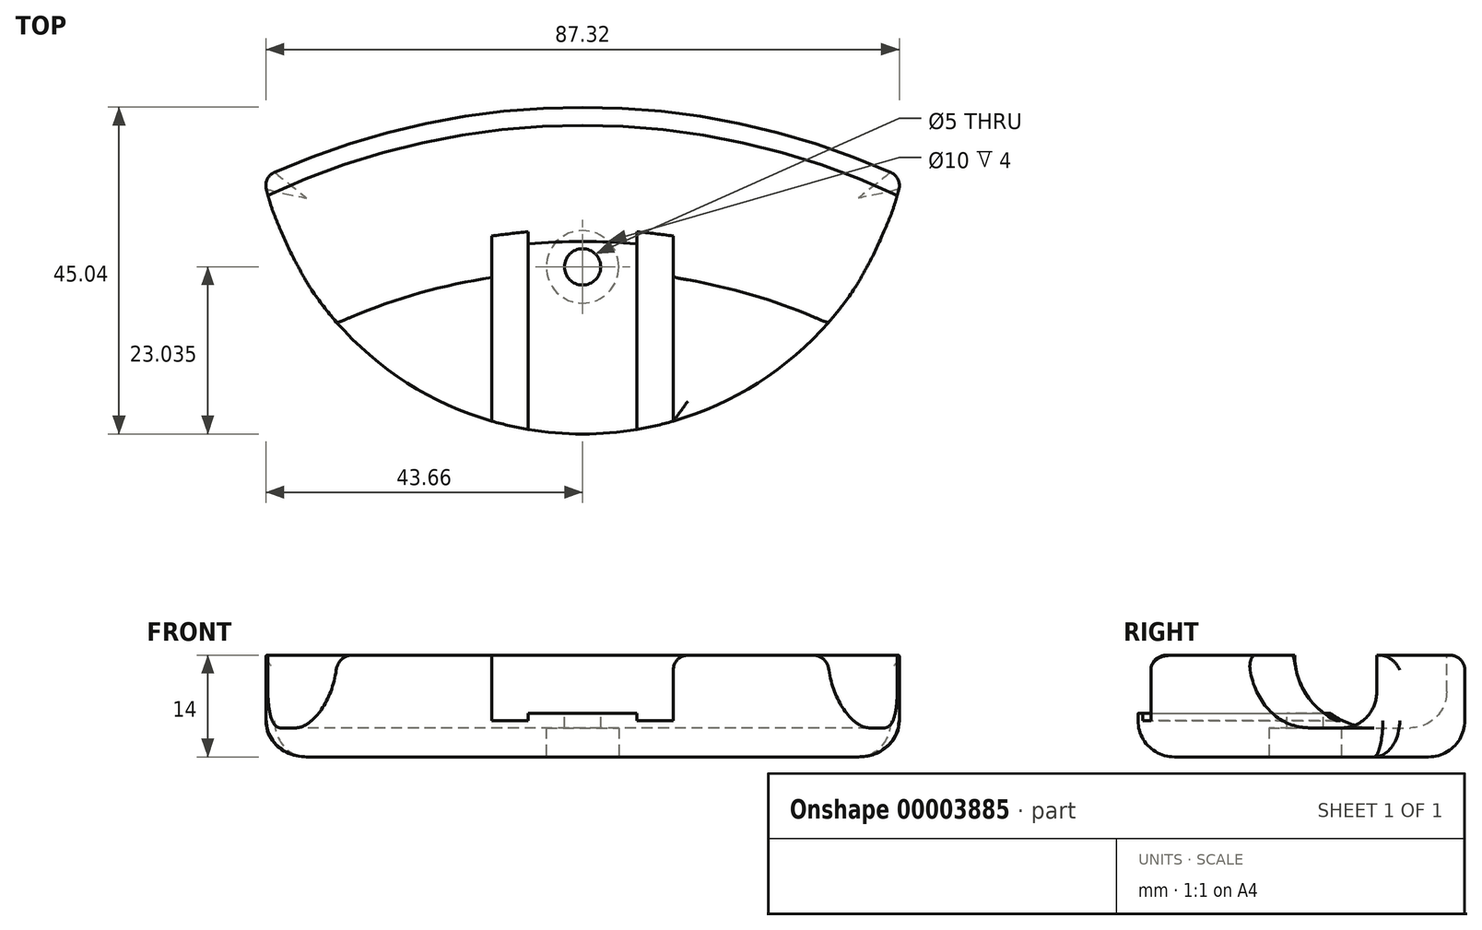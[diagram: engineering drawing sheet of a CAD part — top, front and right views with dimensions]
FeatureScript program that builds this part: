
annotation { "Feature Type Name" : "Feature", "Feature Type Description" : "" }
export const myFeature = defineFeature(function(context is Context, id is Id, definition is map)
    precondition{}
    {
        {
            var Q0;
            Q0=qCreatedBy(makeId("Top.planeOp"),FACE);
            var sketch = newSketch(context, id + "F0", { "sketchPlane" : qUnion([Q0])});
            skLineSegment(sketch, "E0.bottom", {"start": v(-12.5, 20) * mm, "end": v(12.5, 20) * mm});
            skLineSegment(sketch, "E0.top", {"start": v(-12.5, -20) * mm, "end": v(12.5, -20) * mm});
            skLineSegment(sketch, "E0.left", {"start": v(-12.5, 20) * mm, "end": v(-12.5, -20) * mm});
            skLineSegment(sketch, "E0.right", {"start": v(12.5, 20) * mm, "end": v(12.5, -20) * mm});
            skArc(sketch, "E1", {"start": v(43.99, 13.6) * mm, "mid": v(0, 23.27) * mm, "end": v(-43.99, 13.6) * mm});
            skArc(sketch, "E2", {"start": v(-43.99, 13.6) * mm, "mid": v(0, -21.77) * mm, "end": v(43.99, 13.6) * mm});
            skPoint(sketch, "E3", {"position": v(-43.99, 13.6) * mm});
            skPoint(sketch, "E4", {"position": v(43.99, 13.6) * mm});
            skPoint(sketch, "E5", {"position": v(-43.37, 11.14) * mm});
            skPoint(sketch, "E6", {"position": v(43.37, 11.14) * mm});
            skArc(sketch, "E7.trimOffspring", {"start": v(43.37, 11.14) * mm, "mid": v(0, 20.77) * mm, "end": v(-43.37, 11.14) * mm});
            skLineSegment(sketch, "E8", {"start": v(0, 20) * mm, "end": v(0, -20) * mm, "construction": true});
            skArc(sketch, "E9", {"start": v(33.81, -6.48) * mm, "mid": v(0, 0.77) * mm, "end": v(-33.81, -6.48) * mm});
            skPoint(sketch, "E10", {"position": v(0, 1.27) * mm});
            skCircle(sketch, "E11", {"center": v(0, 1.27) * mm, "radius": 2.5 * mm});
            skLineSegment(sketch, "E12", {"start": v(-7.5, -12.17) * mm, "end": v(7.5, -12.17) * mm, "construction": true});
            skPoint(sketch, "E13", {"position": v(0, -12.17) * mm});
            skLineSegment(sketch, "E14", {"start": v(-7.5, -21.14) * mm, "end": v(-7.5, 10.15) * mm});
            skLineSegment(sketch, "E15", {"start": v(7.5, -21.14) * mm, "end": v(7.5, 10.15) * mm});
            skLineSegment(sketch, "E16", {"start": v(-7.5, 10.15) * mm, "end": v(7.5, 10.15) * mm});
            skSolve(sketch);
        }
        {
            var Q0;
            Q0=makeQuery(id+"F0.imprint","IMPRINT",FACE,{"disambiguationData":[TD([[makeQuery(id+"F0.imprint","IMPRINT",EDGE,{"derivedFrom":sQuery(id+"F0.wireOp",EDGE,"E1")}),1.0]])]});
            var Q1;
            {var subQ1=sQuery(id+"F0.wireOp",EDGE,"E7.trimOffspring");Q1=makeQuery(id+"F0.imprint","IMPRINT",FACE,{"disambiguationData":[TD([[makeQuery(id+"F0.imprint","IMPRINT",EDGE,{"derivedFrom":subQ1}),1.0]])]});}
            var Q2;
            {var subQ0=sQuery(id+"F0.wireOp",EDGE,"E9");Q2=makeQuery(id+"F0.imprint","IMPRINT",FACE,{"disambiguationData":[TD([[makeQuery(id+"F0.imprint","IMPRINT",EDGE,{"derivedFrom":subQ0}),1.0]])]});}
            var Q3;
            {var subQ5=sQuery(id+"F0.wireOp",EDGE,"E0.top");Q3=makeQuery(id+"F0.imprint","IMPRINT",FACE,{"disambiguationData":[TD([[makeQuery(id+"F0.imprint","IMPRINT",EDGE,{"derivedFrom":subQ5}),1.0]])]});}
            var Q4;
            {var subQ1=sQuery(id+"F0.wireOp",EDGE,"E0.top");Q4=makeQuery(id+"F0.imprint","IMPRINT",FACE,{"disambiguationData":[TD([[makeQuery(id+"F0.imprint","IMPRINT",EDGE,{"derivedFrom":subQ1}),-1.0]])]});}
            var Q5;
            {var subQ3=sQuery(id+"F0.wireOp",EDGE,"E2");var subQ5=sQuery(id+"F0.wireOp",EDGE,"E7.trimOffspring");var subQ6=makeQuery(id+"F0.imprint","INTERSECT",VERTEX,{"disambiguationData":[OD(0.0)],"derivedFrom":[subQ3,subQ5]});Q5=makeQuery(id+"F0.imprint","IMPRINT",FACE,{"disambiguationData":[TD([[makeQuery(id+"F0.imprint","IMPRINT",EDGE,{"disambiguationData":[TD([[subQ6,1.0]])],"derivedFrom":subQ3}),1.0]])]});}
            var Q6;
            {var subQ5=sQuery(id+"F0.wireOp",EDGE,"E0.bottom");Q6=makeQuery(id+"F0.imprint","IMPRINT",FACE,{"disambiguationData":[TD([[makeQuery(id+"F0.imprint","IMPRINT",EDGE,{"derivedFrom":subQ5}),-1.0]])]});}
            var Q7;
            {var subQ3=sQuery(id+"F0.wireOp",EDGE,"E2");var subQ5=sQuery(id+"F0.wireOp",EDGE,"E7.trimOffspring");var subQ6=makeQuery(id+"F0.imprint","INTERSECT",VERTEX,{"disambiguationData":[OD(1.0)],"derivedFrom":[subQ3,subQ5]});Q7=makeQuery(id+"F0.imprint","IMPRINT",FACE,{"disambiguationData":[TD([[makeQuery(id+"F0.imprint","IMPRINT",EDGE,{"disambiguationData":[TD([[subQ6,-1.0]])],"derivedFrom":subQ3}),1.0]])]});}
            var Q8;
            {var subQ0=sQuery(id+"F0.wireOp",EDGE,"E11");var subQ1=sQuery(id+"F0.wireOp",EDGE,"E9");var subQ3=makeQuery(id+"F0.imprint","INTERSECT",VERTEX,{"disambiguationData":[OD(0.0)],"derivedFrom":[subQ1,subQ0]});Q8=makeQuery(id+"F0.imprint","IMPRINT",FACE,{"disambiguationData":[TD([[makeQuery(id+"F0.imprint","IMPRINT",EDGE,{"disambiguationData":[TD([[subQ3,-1.0]])],"derivedFrom":subQ1}),-1.0]])]});}
            var Q9;
            {var subQ0=sQuery(id+"F0.wireOp",EDGE,"E11");var subQ1=sQuery(id+"F0.wireOp",EDGE,"E9");var subQ3=makeQuery(id+"F0.imprint","INTERSECT",VERTEX,{"disambiguationData":[OD(0.0)],"derivedFrom":[subQ1,subQ0]});Q9=makeQuery(id+"F0.imprint","IMPRINT",FACE,{"disambiguationData":[TD([[makeQuery(id+"F0.imprint","IMPRINT",EDGE,{"disambiguationData":[TD([[subQ3,-1.0]])],"derivedFrom":subQ1}),1.0]])]});}
            var Q10;
            {var subQ0=sQuery(id+"F0.wireOp",EDGE,"E9");var subQ3=sQuery(id+"F0.wireOp",EDGE,"E2");var subQ4=makeQuery(id+"F0.imprint","INTERSECT",VERTEX,{"disambiguationData":[OD(1.0)],"derivedFrom":[subQ3,subQ0]});Q10=makeQuery(id+"F0.imprint","IMPRINT",FACE,{"disambiguationData":[TD([[makeQuery(id+"F0.imprint","IMPRINT",EDGE,{"disambiguationData":[TD([[subQ4,1.0]])],"derivedFrom":subQ0}),1.0]])]});}
            var Q11;
            {var subQ0=sQuery(id+"F0.wireOp",EDGE,"E9");var subQ3=sQuery(id+"F0.wireOp",EDGE,"E2");var subQ4=makeQuery(id+"F0.imprint","INTERSECT",VERTEX,{"disambiguationData":[OD(0.0)],"derivedFrom":[subQ3,subQ0]});Q11=makeQuery(id+"F0.imprint","IMPRINT",FACE,{"disambiguationData":[TD([[makeQuery(id+"F0.imprint","IMPRINT",EDGE,{"disambiguationData":[TD([[subQ4,-1.0]])],"derivedFrom":subQ0}),1.0]])]});}
            var Q12;
            {var subQ4=sQuery(id+"F0.wireOp",EDGE,"f2ed5ddf-1e71-4b46-be9b-5d21263913f5.bottom");Q12=makeQuery(id+"F0.imprint","IMPRINT",FACE,{"disambiguationData":[TD([[makeQuery(id+"F0.imprint","IMPRINT",EDGE,{"derivedFrom":subQ4}),-1.0]])]});}
            var Q13;
            {var subQ0=sQuery(id+"F0.wireOp",EDGE,"f2ed5ddf-1e71-4b46-be9b-5d21263913f5.top");Q13=makeQuery(id+"F0.imprint","IMPRINT",FACE,{"disambiguationData":[TD([[makeQuery(id+"F0.imprint","IMPRINT",EDGE,{"derivedFrom":subQ0}),1.0]])]});}
            var Q14;
            {var subQ1=sQuery(id+"F0.wireOp",EDGE,"E0.bottom");var subQ5=sQuery(id+"F0.wireOp",EDGE,"E14");var subQ6=makeQuery(id+"F0.imprint","INTERSECT",VERTEX,{"derivedFrom":[subQ1,subQ5]});Q14=makeQuery(id+"F0.imprint","IMPRINT",FACE,{"disambiguationData":[TD([[makeQuery(id+"F0.imprint","IMPRINT",EDGE,{"disambiguationData":[TD([[subQ6,-1.0]])],"derivedFrom":subQ1}),1.0]])]});}
            var Q15;
            {var subQ3=sQuery(id+"F0.wireOp",EDGE,"E0.bottom");var subQ8=sQuery(id+"F0.wireOp",EDGE,"E14");var subQ10=makeQuery(id+"F0.imprint","INTERSECT",VERTEX,{"derivedFrom":[subQ3,subQ8]});Q15=makeQuery(id+"F0.imprint","IMPRINT",FACE,{"disambiguationData":[TD([[makeQuery(id+"F0.imprint","IMPRINT",EDGE,{"disambiguationData":[TD([[subQ10,-1.0]])],"derivedFrom":subQ3}),-1.0]])]});}
            var Q16;
            {var subQ3=sQuery(id+"F0.wireOp",EDGE,"E0.top");var subQ5=sQuery(id+"F0.wireOp",EDGE,"E14");var subQ7=makeQuery(id+"F0.imprint","INTERSECT",VERTEX,{"derivedFrom":[subQ3,subQ5]});Q16=makeQuery(id+"F0.imprint","IMPRINT",FACE,{"disambiguationData":[TD([[makeQuery(id+"F0.imprint","IMPRINT",EDGE,{"disambiguationData":[TD([[subQ7,-1.0]])],"derivedFrom":subQ3}),1.0]])]});}
            var Q17;
            {var subQ0=sQuery(id+"F0.wireOp",EDGE,"E14");var subQ1=sQuery(id+"F0.wireOp",EDGE,"E0.top");var subQ2=makeQuery(id+"F0.imprint","INTERSECT",VERTEX,{"derivedFrom":[subQ1,subQ0]});Q17=makeQuery(id+"F0.imprint","IMPRINT",FACE,{"disambiguationData":[TD([[makeQuery(id+"F0.imprint","IMPRINT",EDGE,{"disambiguationData":[TD([[subQ2,-1.0]])],"derivedFrom":subQ1}),-1.0]])]});}
            var Q18;
            {var subQ3=sQuery(id+"F0.wireOp",EDGE,"E16");Q18=makeQuery(id+"F0.imprint","IMPRINT",FACE,{"disambiguationData":[TD([[makeQuery(id+"F0.imprint","IMPRINT",EDGE,{"derivedFrom":subQ3}),-1.0]])]});}
            extrude(context, id + "F1", {"entities" : qUnion([Q0, Q1, Q2, Q3, Q4, Q5, Q6, Q7, Q8, Q9, Q10, Q11, Q12, Q13, Q14, Q15, Q16, Q17, Q18]), "oppositeDirection" : true, "depth" : 14 * mm});
        }
        {
            var Q0;
            {var subQ1=sQuery(id+"F0.wireOp",EDGE,"E7.trimOffspring");Q0=makeQuery(id+"F0.imprint","IMPRINT",FACE,{"disambiguationData":[TD([[makeQuery(id+"F0.imprint","IMPRINT",EDGE,{"derivedFrom":subQ1}),1.0]])]});}
            var Q1;
            {var subQ3=sQuery(id+"F0.wireOp",EDGE,"E2");var subQ5=sQuery(id+"F0.wireOp",EDGE,"E7.trimOffspring");var subQ6=makeQuery(id+"F0.imprint","INTERSECT",VERTEX,{"disambiguationData":[OD(0.0)],"derivedFrom":[subQ3,subQ5]});Q1=makeQuery(id+"F0.imprint","IMPRINT",FACE,{"disambiguationData":[TD([[makeQuery(id+"F0.imprint","IMPRINT",EDGE,{"disambiguationData":[TD([[subQ6,1.0]])],"derivedFrom":subQ3}),1.0]])]});}
            var Q2;
            {var subQ5=sQuery(id+"F0.wireOp",EDGE,"E0.bottom");Q2=makeQuery(id+"F0.imprint","IMPRINT",FACE,{"disambiguationData":[TD([[makeQuery(id+"F0.imprint","IMPRINT",EDGE,{"derivedFrom":subQ5}),-1.0]])]});}
            var Q3;
            {var subQ3=sQuery(id+"F0.wireOp",EDGE,"E2");var subQ5=sQuery(id+"F0.wireOp",EDGE,"E7.trimOffspring");var subQ6=makeQuery(id+"F0.imprint","INTERSECT",VERTEX,{"disambiguationData":[OD(1.0)],"derivedFrom":[subQ3,subQ5]});Q3=makeQuery(id+"F0.imprint","IMPRINT",FACE,{"disambiguationData":[TD([[makeQuery(id+"F0.imprint","IMPRINT",EDGE,{"disambiguationData":[TD([[subQ6,-1.0]])],"derivedFrom":subQ3}),1.0]])]});}
            var Q4;
            {var subQ4=sQuery(id+"F0.wireOp",EDGE,"f2ed5ddf-1e71-4b46-be9b-5d21263913f5.bottom");Q4=makeQuery(id+"F0.imprint","IMPRINT",FACE,{"disambiguationData":[TD([[makeQuery(id+"F0.imprint","IMPRINT",EDGE,{"derivedFrom":subQ4}),-1.0]])]});}
            var Q5;
            {var subQ0=sQuery(id+"F0.wireOp",EDGE,"E11");var subQ1=sQuery(id+"F0.wireOp",EDGE,"E9");var subQ3=makeQuery(id+"F0.imprint","INTERSECT",VERTEX,{"disambiguationData":[OD(0.0)],"derivedFrom":[subQ1,subQ0]});Q5=makeQuery(id+"F0.imprint","IMPRINT",FACE,{"disambiguationData":[TD([[makeQuery(id+"F0.imprint","IMPRINT",EDGE,{"disambiguationData":[TD([[subQ3,-1.0]])],"derivedFrom":subQ1}),-1.0]])]});}
            var Q6;
            {var subQ3=sQuery(id+"F0.wireOp",EDGE,"E0.bottom");var subQ8=sQuery(id+"F0.wireOp",EDGE,"E14");var subQ10=makeQuery(id+"F0.imprint","INTERSECT",VERTEX,{"derivedFrom":[subQ3,subQ8]});Q6=makeQuery(id+"F0.imprint","IMPRINT",FACE,{"disambiguationData":[TD([[makeQuery(id+"F0.imprint","IMPRINT",EDGE,{"disambiguationData":[TD([[subQ10,-1.0]])],"derivedFrom":subQ3}),-1.0]])]});}
            var Q7;
            {var subQ3=sQuery(id+"F0.wireOp",EDGE,"E16");Q7=makeQuery(id+"F0.imprint","IMPRINT",FACE,{"disambiguationData":[TD([[makeQuery(id+"F0.imprint","IMPRINT",EDGE,{"derivedFrom":subQ3}),-1.0]])]});}
            extrude(context, id + "F2", {"entities" : qUnion([Q0, Q1, Q2, Q3, Q4, Q5, Q6, Q7]), "operationType" : NewBodyOperationType.REMOVE, "oppositeDirection" : true, "depth" : 10 * mm});
        }
        {
            var Q0;
            {var subQ5=sQuery(id+"F0.wireOp",EDGE,"E0.top");Q0=makeQuery(id+"F0.imprint","IMPRINT",FACE,{"disambiguationData":[TD([[makeQuery(id+"F0.imprint","IMPRINT",EDGE,{"derivedFrom":subQ5}),1.0]])]});}
            var Q1;
            {var subQ1=sQuery(id+"F0.wireOp",EDGE,"E0.top");Q1=makeQuery(id+"F0.imprint","IMPRINT",FACE,{"disambiguationData":[TD([[makeQuery(id+"F0.imprint","IMPRINT",EDGE,{"derivedFrom":subQ1}),-1.0]])]});}
            var Q2;
            {var subQ0=sQuery(id+"F0.wireOp",EDGE,"f2ed5ddf-1e71-4b46-be9b-5d21263913f5.top");Q2=makeQuery(id+"F0.imprint","IMPRINT",FACE,{"disambiguationData":[TD([[makeQuery(id+"F0.imprint","IMPRINT",EDGE,{"derivedFrom":subQ0}),1.0]])]});}
            var Q3;
            {var subQ0=sQuery(id+"F0.wireOp",EDGE,"E11");var subQ1=sQuery(id+"F0.wireOp",EDGE,"E9");var subQ3=makeQuery(id+"F0.imprint","INTERSECT",VERTEX,{"disambiguationData":[OD(0.0)],"derivedFrom":[subQ1,subQ0]});Q3=makeQuery(id+"F0.imprint","IMPRINT",FACE,{"disambiguationData":[TD([[makeQuery(id+"F0.imprint","IMPRINT",EDGE,{"disambiguationData":[TD([[subQ3,-1.0]])],"derivedFrom":subQ1}),1.0]])]});}
            extrude(context, id + "F3", {"entities" : qUnion([Q0, Q1, Q2, Q3]), "operationType" : NewBodyOperationType.REMOVE, "oppositeDirection" : true, "depth" : 9 * mm});
        }
        {
            var Q0;
            Q0=makeQuery(id+"F2.boolean.opBoolean","COPY",EDGE,{"derivedFrom":makeQuery(id+"F2.opExtrude","CAP_EDGE",EDGE,{"disambiguationData":[OSD([sQuery(id+"F0.wireOp",EDGE,"E9")])],"isStart":false})});
            fillet(context, id + "F4", {"entities" : qUnion([Q0]), "radius" : 10 * mm, "tangentPropagation" : true, "allowEdgeOverflow" : false});
        }
        {
            var Q0;
            Q0=makeQuery(id+"F1.opExtrude","CAP_EDGE",EDGE,{"disambiguationData":[OSD([sQuery(id+"F0.wireOp",EDGE,"E2")])],"isStart":false});
            var Q1;
            Q1=makeQuery(id+"F1.opExtrude","CAP_EDGE",EDGE,{"disambiguationData":[OSD([sQuery(id+"F0.wireOp",EDGE,"E1")])],"isStart":false});
            fillet(context, id + "F5", {"entities" : qUnion([Q0, Q1]), "radius" : 5 * mm, "tangentPropagation" : true, "allowEdgeOverflow" : false});
        }
        {
            var Q0;
            Q0=makeQuery(id+"F1.opExtrude","CAP_EDGE",EDGE,{"disambiguationData":[OSD([sQuery(id+"F0.wireOp",EDGE,"E1")])],"isStart":true});
            var Q1;
            {var subQ0=sQuery(id+"F0.wireOp",EDGE,"E2");var subQ1=makeQuery(id+"F2.opExtrude","SWEPT_FACE",FACE,{"disambiguationData":[OSD([sQuery(id+"F0.wireOp",EDGE,"E9")])]});var subQ2=makeQuery(id+"F1.opExtrude","SWEPT_FACE",FACE,{"disambiguationData":[OSD([subQ0])]});var subQ3=makeQuery(id+"F1.opExtrude","CAP_FACE",FACE,{"disambiguationData":[OSD([sQuery(id+"F0.wireOp",EDGE,"E1"),subQ0])],"isStart":true});Q1=makeQuery(id+"F3.boolean.opBoolean","SPLIT",EDGE,{"disambiguationData":[TD([makeQuery(id+"F3.opExtrude","SWEPT_FACE",FACE,{"disambiguationData":[OSD([sQuery(id+"F0.wireOp",EDGE,"E0.left")])]})])],"derivedFrom":makeQuery(id+"F2.boolean.opBoolean","SPLIT",EDGE,{"disambiguationData":[TD([subQ3,subQ2,subQ1])],"derivedFrom":makeQuery(id+"F1.opExtrude","CAP_EDGE",EDGE,{"disambiguationData":[OSD([subQ0])],"isStart":true})})});}
            var Q2;
            {var subQ0=sQuery(id+"F0.wireOp",EDGE,"E2");var subQ1=makeQuery(id+"F2.opExtrude","SWEPT_FACE",FACE,{"disambiguationData":[OSD([sQuery(id+"F0.wireOp",EDGE,"E9")])]});var subQ2=makeQuery(id+"F1.opExtrude","SWEPT_FACE",FACE,{"disambiguationData":[OSD([subQ0])]});var subQ3=makeQuery(id+"F1.opExtrude","CAP_FACE",FACE,{"disambiguationData":[OSD([sQuery(id+"F0.wireOp",EDGE,"E1"),subQ0])],"isStart":true});Q2=makeQuery(id+"F3.boolean.opBoolean","SPLIT",EDGE,{"disambiguationData":[TD([makeQuery(id+"F3.opExtrude","SWEPT_FACE",FACE,{"disambiguationData":[OSD([sQuery(id+"F0.wireOp",EDGE,"E0.right")])]})])],"derivedFrom":makeQuery(id+"F2.boolean.opBoolean","SPLIT",EDGE,{"disambiguationData":[TD([subQ3,subQ2,subQ1])],"derivedFrom":makeQuery(id+"F1.opExtrude","CAP_EDGE",EDGE,{"disambiguationData":[OSD([subQ0])],"isStart":true})})});}
            var Q3;
            Q3=makeQuery(id+"F3.boolean.opBoolean","COPY",EDGE,{"derivedFrom":makeQuery(id+"F3.opExtrude","SWEPT_EDGE",EDGE,{"disambiguationData":[OSD([sQuery(id+"F0.wireOp",EDGE,"E0.top"),sQuery(id+"F0.wireOp",EDGE,"E0.right"),sQuery(id+"F0.wireOp",EDGE,"E2")])]})});
            var Q4;
            Q4=makeQuery(id+"F3.boolean.opBoolean","COPY",EDGE,{"derivedFrom":makeQuery(id+"F3.opExtrude","SWEPT_EDGE",EDGE,{"disambiguationData":[OSD([sQuery(id+"F0.wireOp",EDGE,"E0.top"),sQuery(id+"F0.wireOp",EDGE,"E0.left"),sQuery(id+"F0.wireOp",EDGE,"E2")])]})});
            var Q5;
            Q5=makeQuery(id+"F3.boolean.opBoolean","COPY",EDGE,{"derivedFrom":makeQuery(id+"F3.opExtrude","CAP_EDGE",EDGE,{"disambiguationData":[OSD([sQuery(id+"F0.wireOp",EDGE,"E0.left")])],"isStart":true})});
            var Q6;
            Q6=makeQuery(id+"F3.boolean.opBoolean","COPY",EDGE,{"derivedFrom":makeQuery(id+"F3.opExtrude","CAP_EDGE",EDGE,{"disambiguationData":[OSD([sQuery(id+"F0.wireOp",EDGE,"E0.right")])],"isStart":true})});
            var Q7;
            {var subQ0=sQuery(id+"F0.wireOp",EDGE,"E9");Q7=makeQuery(id+"F3.boolean.opBoolean","SPLIT",EDGE,{"disambiguationData":[TD([makeQuery(id+"F3.opExtrude","SWEPT_FACE",FACE,{"disambiguationData":[OSD([sQuery(id+"F0.wireOp",EDGE,"E0.left")])]})])],"derivedFrom":makeQuery(id+"F2.boolean.opBoolean","COPY",EDGE,{"derivedFrom":makeQuery(id+"F2.opExtrude","CAP_EDGE",EDGE,{"disambiguationData":[OSD([subQ0])],"isStart":true})})});}
            var Q8;
            {var subQ0=sQuery(id+"F0.wireOp",EDGE,"E9");Q8=makeQuery(id+"F3.boolean.opBoolean","SPLIT",EDGE,{"disambiguationData":[TD([makeQuery(id+"F3.opExtrude","SWEPT_FACE",FACE,{"disambiguationData":[OSD([sQuery(id+"F0.wireOp",EDGE,"E0.right")])]})])],"derivedFrom":makeQuery(id+"F2.boolean.opBoolean","COPY",EDGE,{"derivedFrom":makeQuery(id+"F2.opExtrude","CAP_EDGE",EDGE,{"disambiguationData":[OSD([subQ0])],"isStart":true})})});}
            var Q9;
            Q9=makeQuery(id+"F2.boolean.opBoolean","COPY",EDGE,{"derivedFrom":makeQuery(id+"F2.opExtrude","CAP_EDGE",EDGE,{"disambiguationData":[OSD([sQuery(id+"F0.wireOp",EDGE,"E7.trimOffspring")])],"isStart":true})});
            var Q10;
            {var subQ0=sQuery(id+"F0.wireOp",EDGE,"E1");var subQ1=sQuery(id+"F0.wireOp",EDGE,"E2");Q10=makeQuery(id+"F1.opExtrude","SWEPT_EDGE",EDGE,{"disambiguationData":[OSD([subQ0,subQ1]),TDD([makeQuery(id+"F0.imprint","INTERSECT",VERTEX,{"disambiguationData":[OD(1.0)],"derivedFrom":[subQ0,subQ1]})])]});}
            var Q11;
            {var subQ0=sQuery(id+"F0.wireOp",EDGE,"E1");var subQ1=sQuery(id+"F0.wireOp",EDGE,"E2");Q11=makeQuery(id+"F1.opExtrude","SWEPT_EDGE",EDGE,{"disambiguationData":[OSD([subQ0,subQ1]),TDD([makeQuery(id+"F0.imprint","INTERSECT",VERTEX,{"disambiguationData":[OD(0.0)],"derivedFrom":[subQ0,subQ1]})])]});}
            fillet(context, id + "F6", {"entities" : qUnion([Q0, Q1, Q2, Q3, Q4, Q5, Q6, Q7, Q8, Q9, Q10, Q11]), "radius" : 2 * mm, "tangentPropagation" : true, "allowEdgeOverflow" : false});
        }
        {
            var Q0;
            Q0=makeQuery(id+"F2.boolean.opBoolean","COPY",EDGE,{"derivedFrom":makeQuery(id+"F2.opExtrude","CAP_EDGE",EDGE,{"disambiguationData":[OSD([sQuery(id+"F0.wireOp",EDGE,"E7.trimOffspring")])],"isStart":false})});
            fillet(context, id + "F7", {"entities" : qUnion([Q0]), "radius" : 5 * mm, "tangentPropagation" : true, "allowEdgeOverflow" : false});
        }
        {
            var Q0;
            {var subQ0=sQuery(id+"F0.wireOp",EDGE,"E11");var subQ1=sQuery(id+"F0.wireOp",EDGE,"E9");var subQ3=makeQuery(id+"F0.imprint","INTERSECT",VERTEX,{"disambiguationData":[OD(0.0)],"derivedFrom":[subQ1,subQ0]});Q0=makeQuery(id+"F0.imprint","IMPRINT",FACE,{"disambiguationData":[TD([[makeQuery(id+"F0.imprint","IMPRINT",EDGE,{"disambiguationData":[TD([[subQ3,-1.0]])],"derivedFrom":subQ1}),-1.0]])]});}
            var Q1;
            {var subQ0=sQuery(id+"F0.wireOp",EDGE,"E11");var subQ1=sQuery(id+"F0.wireOp",EDGE,"E9");var subQ3=makeQuery(id+"F0.imprint","INTERSECT",VERTEX,{"disambiguationData":[OD(0.0)],"derivedFrom":[subQ1,subQ0]});Q1=makeQuery(id+"F0.imprint","IMPRINT",FACE,{"disambiguationData":[TD([[makeQuery(id+"F0.imprint","IMPRINT",EDGE,{"disambiguationData":[TD([[subQ3,-1.0]])],"derivedFrom":subQ1}),1.0]])]});}
            extrude(context, id + "F8", {"entities" : qUnion([Q0, Q1]), "operationType" : NewBodyOperationType.REMOVE, "endBound" : BoundingType.THROUGH_ALL, "oppositeDirection" : true, "depth" : 20 * mm});
        }
        {
            var Q0;
            Q0=makeQuery(id+"F1.opExtrude","CAP_FACE",FACE,{"disambiguationData":[OSD([sQuery(id+"F0.wireOp",EDGE,"E1"),sQuery(id+"F0.wireOp",EDGE,"E2")])],"isStart":false});
            var sketch = newSketch(context, id + "F9", { "sketchPlane" : qUnion([Q0])});
            skCircle(sketch, "E17", {"center": v(0, -1.27) * mm, "radius": 5 * mm});
            skSolve(sketch);
        }
        {
            var Q0;
            Q0=makeQuery(id+"F9.imprint","IMPRINT",FACE,{"disambiguationData":[TD([[makeQuery(id+"F9.imprint","IMPRINT",EDGE,{"derivedFrom":makeQuery(id+"F8.boolean.opBoolean","INTERSECT",EDGE,{"derivedFrom":[makeQuery(id+"F1.opExtrude","CAP_FACE",FACE,{"disambiguationData":[OSD([sQuery(id+"F0.wireOp",EDGE,"E1"),sQuery(id+"F0.wireOp",EDGE,"E2")])],"isStart":false}),makeQuery(id+"F8.opExtrude","SWEPT_FACE",FACE,{"disambiguationData":[OSD([sQuery(id+"F0.wireOp",EDGE,"E11")])]})]})}),-1.0]])]});
            var Q1;
            Q1=makeQuery(id+"F9.imprint","IMPRINT",FACE,{"disambiguationData":[TD([[makeQuery(id+"F9.imprint","IMPRINT",EDGE,{"derivedFrom":sQuery(id+"F9.wireOp",EDGE,"E17")}),1.0]])]});
            extrude(context, id + "F10", {"entities" : qUnion([Q0, Q1]), "operationType" : NewBodyOperationType.REMOVE, "oppositeDirection" : true, "depth" : 4 * mm});
        }
        {
            var Q0;
            {var subQ3=sQuery(id+"F0.wireOp",EDGE,"E0.top");var subQ5=sQuery(id+"F0.wireOp",EDGE,"E14");var subQ7=makeQuery(id+"F0.imprint","INTERSECT",VERTEX,{"derivedFrom":[subQ3,subQ5]});Q0=makeQuery(id+"F0.imprint","IMPRINT",FACE,{"disambiguationData":[TD([[makeQuery(id+"F0.imprint","IMPRINT",EDGE,{"disambiguationData":[TD([[subQ7,-1.0]])],"derivedFrom":subQ3}),1.0]])]});}
            var Q1;
            {var subQ3=sQuery(id+"F0.wireOp",EDGE,"E16");Q1=makeQuery(id+"F0.imprint","IMPRINT",FACE,{"disambiguationData":[TD([[makeQuery(id+"F0.imprint","IMPRINT",EDGE,{"derivedFrom":subQ3}),-1.0]])]});}
            var Q2;
            {var subQ1=sQuery(id+"F0.wireOp",EDGE,"E0.top");var subQ5=sQuery(id+"F0.wireOp",EDGE,"E14");var subQ6=makeQuery(id+"F0.imprint","INTERSECT",VERTEX,{"derivedFrom":[subQ1,subQ5]});Q2=makeQuery(id+"F0.imprint","IMPRINT",FACE,{"disambiguationData":[TD([[makeQuery(id+"F0.imprint","IMPRINT",EDGE,{"disambiguationData":[TD([[subQ6,-1.0]])],"derivedFrom":subQ1}),-1.0]])]});}
            extrude(context, id + "F11", {"entities" : qUnion([Q0, Q1, Q2]), "operationType" : NewBodyOperationType.REMOVE, "oppositeDirection" : true, "depth" : 8 * mm});
        }
    });
